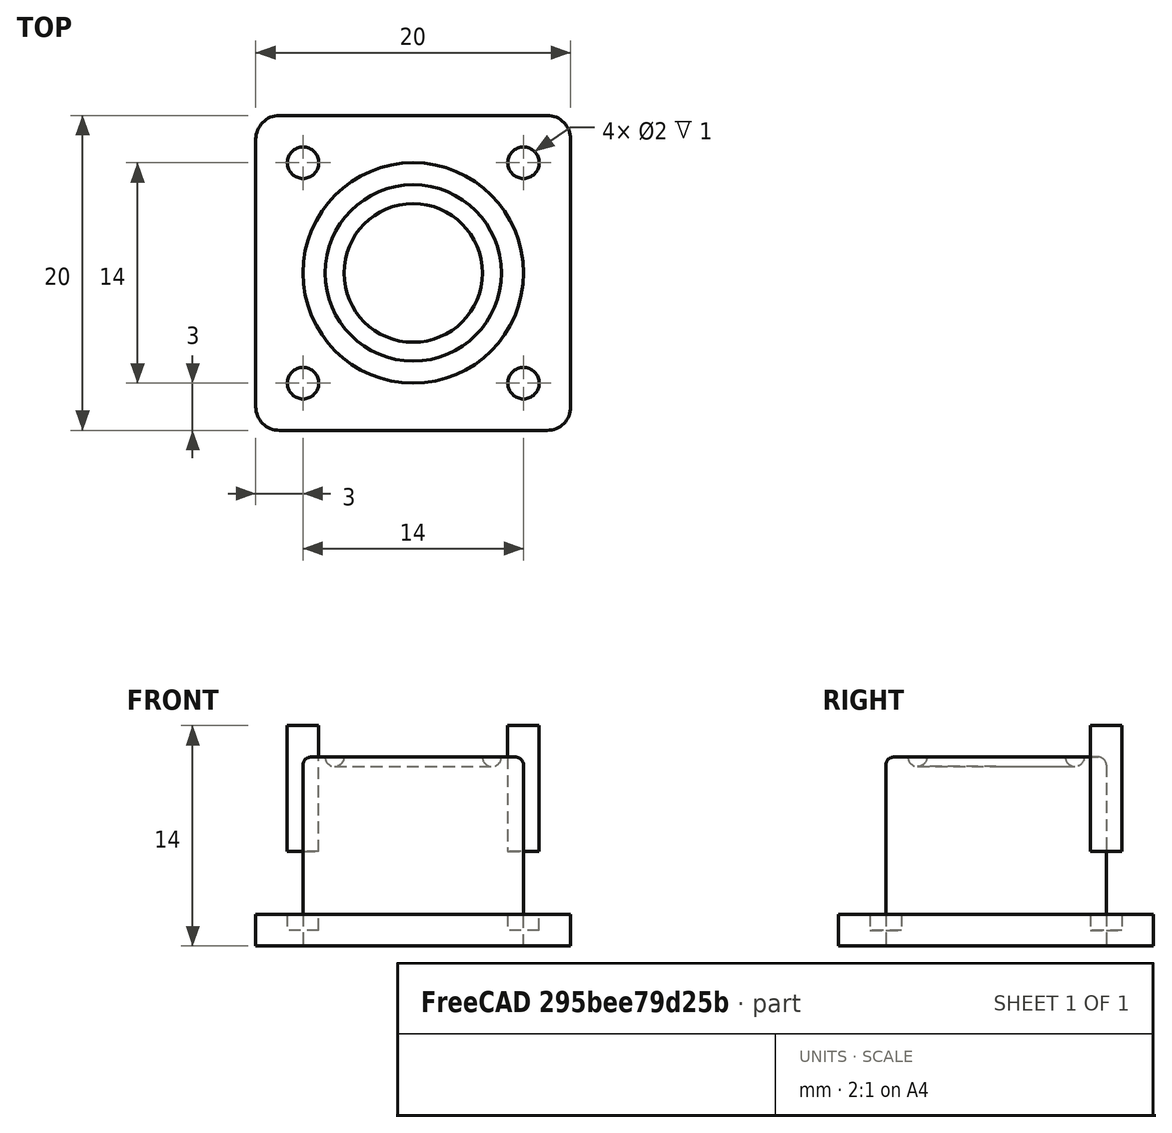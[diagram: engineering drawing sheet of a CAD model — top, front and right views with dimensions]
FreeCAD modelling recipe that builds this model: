
FCSTD DOCUMENT  (FreeCAD 0.21R33694 (Git))
Label: OJT1_T015R014_pota_de_taula
License: All rights reserved
LicenseURL: http://en.wikipedia.org/wiki/All_rights_reserved
objects: Part::Cylinder×3, Part::Fillet×2, Part::FeaturePython×2, Part::Cut×2, Part::Box×1, Part::MultiFuse×1, Part::Torus×1
note: 10 computed .brp shape members not serialized (recipe doc carries the construction recipe); baked Part::Feature solids carry a one-line shape summary decoded from their .brp

FEATURE [Part::Box] Box  label="Cube"
  AttacherType = Attacher::AttachEngine3D
  Height = 2
  Length = 20
  Width = 20
FEATURE [Part::Fillet] Fillet
  Base = -> Box
  Edges = 4 edges r=1.5: [Edge1,Edge3,Edge5,Edge7]
FEATURE [Part::Cylinder] Cylinder
  Angle = 360
  AttacherType = Attacher::AttachEngine3D
  FirstAngle = 0
  Height = 12
  Placement = pos=(10,10,0) rot=(0,0,1;0rad)
  Radius = 7
  SecondAngle = 0
FEATURE [Part::Cylinder] Cylinder001
  Angle = 360
  AttacherType = Attacher::AttachEngine3D
  FirstAngle = 0
  Height = 8
  Placement = pos=(17,17,6) rot=(0,0,1;0rad)
  Radius = 1
  SecondAngle = 0
FEATURE [Part::FeaturePython] Array  # Draft array (typed FeaturePython)
  AlwaysSyncPlacement = false
  Angle = 360
  ArrayType = 0
  Axis = (0,0,1)
  Base = -> Cylinder001
  Center = (0,0,0)
  Count = 2
  ExpandArray = false
  Fuse = false
  IntervalAxis = (0,0,0)
  IntervalX = (-14,-14,0)
  IntervalY = (-14,-14,0)
  IntervalZ = (0,0,6)
  NumberCircles = 3
  NumberPolar = 4
  NumberX = 2
  NumberY = 0
  NumberZ = 0
  Placement = pos=(0,0,-5) rot=(0,0,1;0rad)
  PlacementList = 2 placements: [(17,17,6),(3,3,6)]
  RadialDistance = 50
  ScaleList = (2) [(1,1,1),(1,1,1)]
  Symmetry = 1
  TangentialDistance = 25
FEATURE [Part::Cylinder] Cylinder002
  Angle = 360
  AttacherType = Attacher::AttachEngine3D
  FirstAngle = 0
  Height = 8
  Placement = pos=(3,17,6) rot=(0,0,1;0rad)
  Radius = 1
  SecondAngle = 0
FEATURE [Part::FeaturePython] Array001  # Draft array (typed FeaturePython)
  AlwaysSyncPlacement = false
  Angle = 360
  ArrayType = 0
  Axis = (0,0,1)
  Base = -> Cylinder002
  Center = (0,0,0)
  Count = 2
  ExpandArray = false
  Fuse = false
  IntervalAxis = (0,0,0)
  IntervalX = (14,-14,0)
  IntervalY = (14,14,0)
  IntervalZ = (0,0,6)
  NumberCircles = 3
  NumberPolar = 4
  NumberX = 2
  NumberY = 0
  NumberZ = 0
  Placement = pos=(0,0,-5) rot=(0,0,1;0rad)
  PlacementList = 2 placements: [(3,17,6),(17,3,6)]
  RadialDistance = 50
  ScaleList = (2) [(1,1,1),(1,1,1)]
  Symmetry = 1
  TangentialDistance = 25
FEATURE [Part::MultiFuse] Fusion
  Refine = true
  Shapes = -> [Array,Array001]
FEATURE [Part::Cut] Cut
  Base = -> Fillet
  Refine = true
  Tool = -> Fusion
FEATURE [Part::Fillet] Fillet001
  Base = -> Cylinder
  Edges = 1 edges r=0.5: [Edge3]
FEATURE [Part::Torus] Torus
  Angle1 = -180
  Angle2 = 180
  Angle3 = 360
  AttacherType = Attacher::AttachEngine3D
  Placement = pos=(10,10,12) rot=(0,0,1;0rad)
  Radius1 = 5
  Radius2 = 0.6
FEATURE [Part::Cut] Cut001
  Base = -> Fillet001
  Refine = true
  Tool = -> Torus
